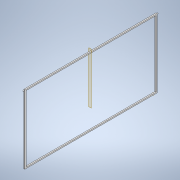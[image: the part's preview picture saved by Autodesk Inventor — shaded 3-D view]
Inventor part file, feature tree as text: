
AUTODESK INVENTOR PART (.ipt)
format: ipt  version: 2022 (Build 260153000, 153)  size: 156,160 bytes
history: native  units: mm
features: extrude x7, sketch x7, projected_geometry x3, plane x2, mirror x2, fillet x1
ambient origin geometry x8: Origin, YZ Plane, XZ Plane, XY Plane, X Axis, Y Axis, Z Axis, Center Point
bodies: Solid1 (feature_tree)
feature tree (22):
  extrude  "Extrusion1"  Depth=10.0mm
  extrude  "Extrusion2"  Depth=10.0mm
  plane  "Work Plane1"
  mirror  "Mirror1"
  fillet  "Fillet1"  [1 undecoded]
  plane  "Work Plane2"
  extrude  "Extrusion3"  Depth=35.0mm TaperAngle=0.0deg
  extrude  "Extrusion4"  Depth=10.0mm
  extrude  "Extrusion5"  Depth=15.0mm TaperAngle=0.0deg
  extrude  "Extrusion6"  Depth=10.0mm TaperAngle=0.0deg
  extrude  "Extrusion7"  Depth=10.0mm TaperAngle=0.0deg
  mirror  "Mirror2"
  sketch  "Sketch1"  dims[d0=490.0mm d2=10.0mm]
  sketch  "Sketch2"  dims[d3=10.0mm d4=0.0mm d5=4.5mm d6=135.0deg]
  projected_geometry  "Projected Loop1"
  sketch  "Sketch3"  dims[d7=1.0mm d8=35.0mm d9=0.0mm]
  sketch  "Sketch4"  dims[d10=10.0mm d11=2.0mm]
  sketch  "Sketch5"  dims[d12=-10.0mm d13=15.0mm d14=0.0mm]
  sketch  "Sketch6"  dims[d15=10.0mm d16=0.0mm d17=10.0mm d18=0.0mm]
  projected_geometry  "Projected Loop2"
  sketch  "Sketch7"  dims[d19=5.0mm d20=10.0mm d21=0.0mm d22=10.0mm d23=5.0mm d24=0.0mm]
  projected_geometry  "Projected Loop3"
note: 1 required parameter value undecoded (feature->parameter linkage not recoverable at this tier; creation-order binding heuristic only, values carry confidence <= 0.55)
